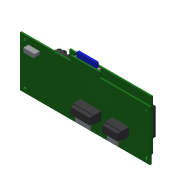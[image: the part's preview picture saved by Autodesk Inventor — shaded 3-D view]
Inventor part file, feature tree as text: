
AUTODESK INVENTOR PART (.ipt)
format: ipt  version: 2016 (Build 200138000, 138)  size: 691,712 bytes
history: native  units: mm
features: extrude x17, sketch x17, fillet x4, projected_geometry x2, plane x1, chamfer x1, pattern_circular x1, other x1
ambient origin geometry x8: Origin, YZ Plane, XZ Plane, XY Plane, X Axis, Y Axis, Z Axis, Center Point
bodies: Solid1 (feature_tree), Solid2 (feature_tree), Solid3 (feature_tree), Solid4 (feature_tree), Solid5 (feature_tree), Solid6 (feature_tree), Solid7 (feature_tree), Solid8 (feature_tree)
feature tree (44):
  extrude  "Extrusion1"  Depth=60.0mm
  plane  "Work Plane1"
  extrude  "Extrusion2"  Depth=6.0mm
  extrude  "Extrusion3"  Depth=60.0mm
  extrude  "Extrusion4"  Depth=5.0mm
  extrude  "Extrusion5"  Depth=3.2mm
  extrude  "Extrusion6"  Depth=5.0mm
  chamfer  "Chamfer1"  Distance=5.0mm
  fillet  "Fillet1"  Radius=5.0mm
  extrude  "Extrusion7"  Depth=5.0mm
  pattern_circular  "Circular Pattern1"  Count=3  [1 undecoded]
  fillet  "Fillet2"  Radius=30.0mm
  sketch  "Sketch8"  dims[d19=5.0mm]
  extrude  "Extrusion8"  Depth=17.0mm TaperAngle=0.0deg
  extrude  "Extrusion9"  Depth=10.0mm TaperAngle=0.0deg
  extrude  "Extrusion10"  Depth=28.5mm
  extrude  "Extrusion11"  Depth=10.0mm
  extrude  "Extrusion12"  Depth=10.0mm
  fillet  "Fillet3"  Radius=3.0mm
  extrude  "Extrusion13"  Depth=10.0mm TaperAngle=45.0deg
  fillet  "Fillet4"  Radius=6.0mm
  extrude  "Extrusion14"  TaperAngle=0.0deg  [1 undecoded]
  extrude  "Extrusion15"  Depth=10.0mm TaperAngle=360.0deg
  extrude  "Extrusion16"  Depth=3.0mm
  extrude  "Extrusion17"  Depth=10.0mm
  sketch  "Sketch1"  dims[d0=155.0mm d1=60.0mm]
  sketch  "Sketch2"  dims[d2=1.8mm d3=0.0mm d4=6.0mm]
  sketch  "Sketch3"  dims[d5=35.0mm d6=60.0mm]
  sketch  "Sketch4"  dims[d7=3.2mm d8=5.0mm d9=5.0mm]
  sketch  "Sketch5"  dims[d10=3.2mm d11=3.2mm]
  sketch  "Sketch6"  dims[d12=3.2mm d13=5.0mm d14=5.0mm d15=5.0mm d16=5.0mm]
  sketch  "Sketch7"  dims[d17=5.0mm d18=5.0mm]
  sketch  "Sketch9"  dims[d20=5.0mm]
  sketch  "Sketch10"  dims[d21=10.0mm]
  sketch  "Sketch11"  dims[d23=98.0mm]
  sketch  "Sketch12"  dims[d24=1.8mm d25=0.0mm]
  sketch  "Sketch13"  dims[d26=13.0mm]
  sketch  "Sketch15"  dims[d27=12.5mm]
  sketch  "Sketch16"  dims[d28=6.0mm d29=0.0mm d30=30.0mm d31=30.0mm]
  projected_geometry  "Projected Loop2"
  sketch  "Sketch17"  dims[d32=6.0mm d33=17.0mm d34=0.0mm]
  projected_geometry  "Projected Loop3"
  sketch  "Sketch18"  dims[d35=30.0mm d36=8.5mm d37=0.0mm d38=28.5mm d39=30.0mm d40=3.25mm d41=3.0mm d42=0.0mm d43=4.0mm d44=2.0mm d45=45.0deg d46=6.0mm d47=0.0mm d48=0.0mm d49=140.0mm d50=360.0deg d52=3.0mm d53=24.0mm d54=2.5mm d55=2.25mm d56=6.0mm d57=0.0mm d58=94.0mm d59=32.0mm d60=2.0mm d61=5.0mm d62=0.0mm d63=77.0mm d64=25.0mm d65=8.5mm d66=0.5mm d67=0.0mm d68=1.0mm d69=0.0mm d70=10.0mm d71=0.0mm d72=20.0mm d73=2.5mm d74=0.0mm d75=1.0mm d76=3.0mm d77=3.0mm d78=3.0mm d79=1.0mm d80=0.1mm d81=4.0mm d82=0.1mm d83=0.0mm d84=4.0mm d85=1.0mm d86=1.0mm d92=17.0mm d93=10.0mm d95=17.0mm d96=10.0mm d97=20.0mm d98=25.0mm d99=13.0mm d100=0.0mm d101=10.2mm d102=10.2mm d103=1.4mm d104=1.4mm d105=4.0mm d106=4.0mm d107=4.0mm d108=4.0mm d109=13.0mm d110=0.0mm d111=1.0mm d112=1.0mm d113=13.0mm d114=0.0mm d115=25.0mm d116=83.0mm d117=1.5mm d118=5.0mm d119=13.5mm d120=135.0deg d121=8.0mm d122=10.0mm d138=6.0mm d139=0.0mm]
  other  "Image1"
note: 2 required parameter values undecoded (feature->parameter linkage not recoverable at this tier; creation-order binding heuristic only, values carry confidence <= 0.55)
